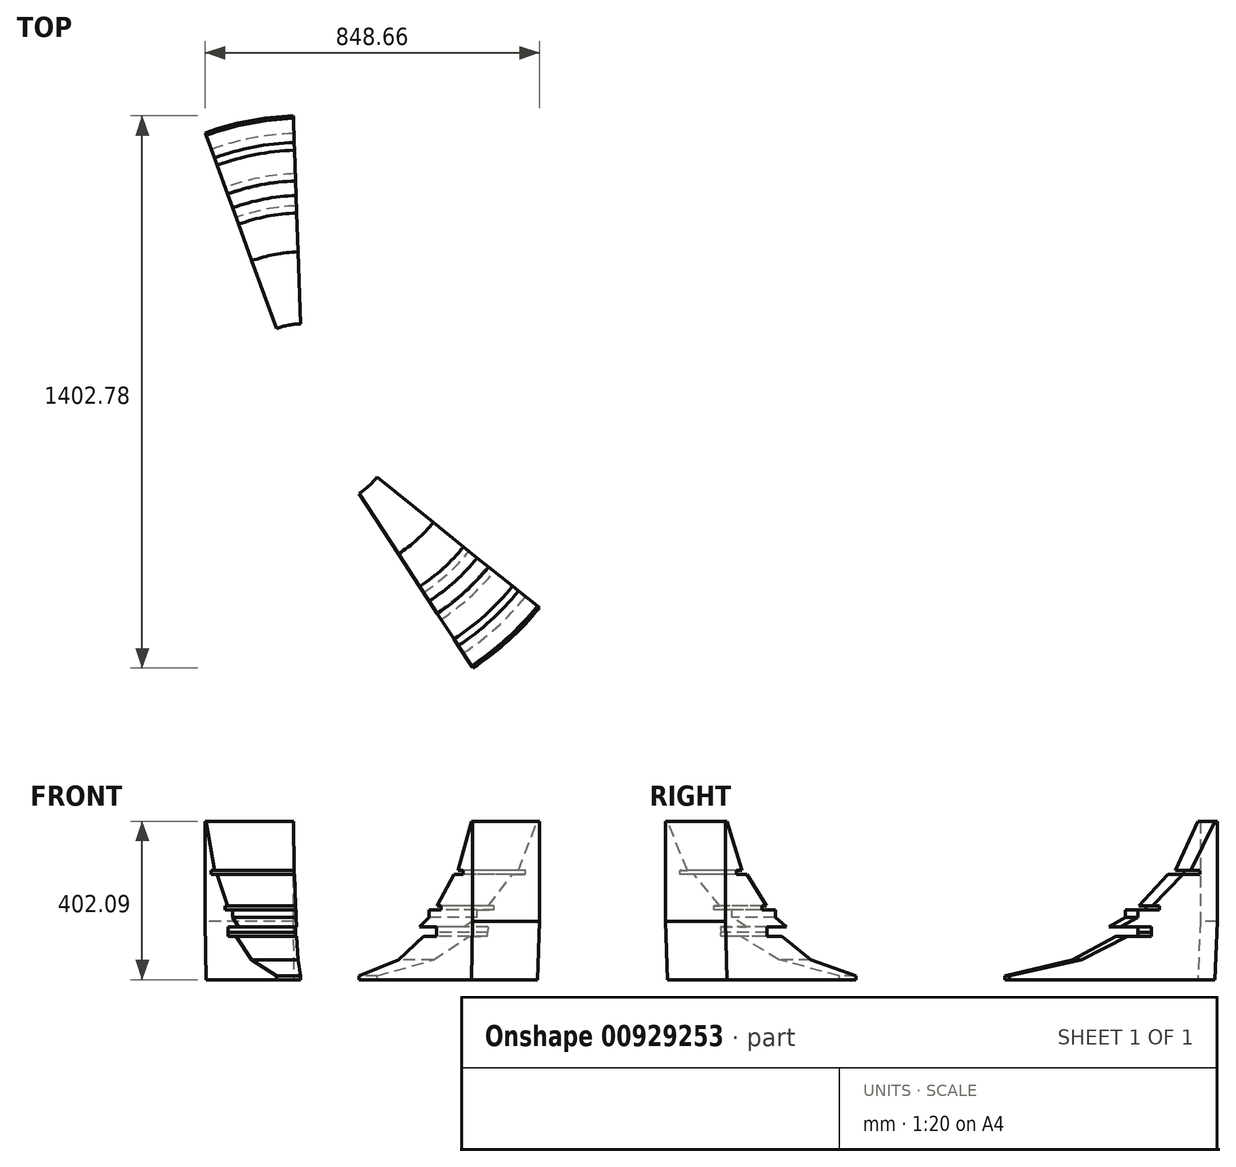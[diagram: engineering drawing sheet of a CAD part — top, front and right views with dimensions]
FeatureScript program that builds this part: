
annotation { "Feature Type Name" : "Feature", "Feature Type Description" : "" }
export const myFeature = defineFeature(function(context is Context, id is Id, definition is map)
    precondition{}
    {
        {
            var Q0;
            Q0=qCreatedBy(makeId("Front.planeOp"),FACE);
            var sketch = newSketch(context, id + "F0", { "sketchPlane" : qUnion([Q0])});
            skLineSegment(sketch, "E0", {"start": v(0, 0) * mm, "end": v(120, 0) * mm});
            skLineSegment(sketch, "E1", {"start": v(120, 0) * mm, "end": v(120, 10) * mm});
            skLineSegment(sketch, "E2.bottom", {"start": v(120, 10) * mm, "end": v(420, 10) * mm, "construction": true});
            skLineSegment(sketch, "E2.top", {"start": v(120, 110) * mm, "end": v(420, 110) * mm, "construction": true});
            skLineSegment(sketch, "E2.left", {"start": v(120, 10) * mm, "end": v(120, 110) * mm, "construction": true});
            skLineSegment(sketch, "E2.right", {"start": v(420, 10) * mm, "end": v(420, 110) * mm, "construction": true});
            skLineSegment(sketch, "E3", {"start": v(120, 10) * mm, "end": v(303.16, 50.16) * mm});
            skLineSegment(sketch, "E4", {"start": v(303.16, 50.16) * mm, "end": v(420, 110) * mm});
            skLineSegment(sketch, "E5", {"start": v(420, 110) * mm, "end": v(480.38, 110) * mm});
            skLineSegment(sketch, "E6", {"start": v(480.38, 110) * mm, "end": v(480.38, 119.71) * mm});
            skLineSegment(sketch, "E7", {"start": v(420, 134) * mm, "end": v(480.73, 134) * mm});
            skLineSegment(sketch, "E8", {"start": v(480.73, 134) * mm, "end": v(480.38, 119.71) * mm});
            skLineSegment(sketch, "E9", {"start": v(420, 134) * mm, "end": v(401.9, 134) * mm});
            skLineSegment(sketch, "E10", {"start": v(401.9, 134) * mm, "end": v(446.37, 158.34) * mm});
            skLineSegment(sketch, "E11", {"start": v(446.37, 158.34) * mm, "end": v(446.37, 177.2) * mm});
            skLineSegment(sketch, "E12", {"start": v(446.37, 177.2) * mm, "end": v(501.62, 177.2) * mm});
            skLineSegment(sketch, "E13", {"start": v(501.62, 177.2) * mm, "end": v(501.62, 187.3) * mm});
            skLineSegment(sketch, "E14", {"start": v(501.62, 187.3) * mm, "end": v(483.43, 187.3) * mm});
            skLineSegment(sketch, "E15", {"start": v(483.43, 187.3) * mm, "end": v(561.58, 268.16) * mm});
            skLineSegment(sketch, "E16", {"start": v(561.58, 268.16) * mm, "end": v(575.06, 268.16) * mm});
            skLineSegment(sketch, "E17", {"start": v(575.06, 268.16) * mm, "end": v(604.03, 268.16) * mm});
            skLineSegment(sketch, "E18", {"start": v(604.03, 268.16) * mm, "end": v(604.03, 277.45) * mm});
            skLineSegment(sketch, "E19", {"start": v(604.03, 277.45) * mm, "end": v(581.12, 277.45) * mm});
            skLineSegment(sketch, "E20", {"start": v(581.12, 277.45) * mm, "end": v(642.43, 402.09) * mm});
            skLineSegment(sketch, "E21", {"start": v(642.43, 402.09) * mm, "end": v(648.86, 402.09) * mm});
            skLineSegment(sketch, "E22", {"start": v(648.86, 402.09) * mm, "end": v(648.86, 148.71) * mm});
            skLineSegment(sketch, "E23", {"start": v(648.86, 148.71) * mm, "end": v(642.43, 0) * mm});
            skLineSegment(sketch, "E24", {"start": v(642.43, 0) * mm, "end": v(355.24, 0) * mm});
            skLineSegment(sketch, "E25", {"start": v(355.24, 0) * mm, "end": v(120, 0) * mm});
            skLineSegment(sketch, "E26", {"start": v(0, 0) * mm, "end": v(0, 125.67) * mm});
            skLineSegment(sketch, "E27", {"start": v(120, 0) * mm, "end": v(-80, 0) * mm});
            skLineSegment(sketch, "E28", {"start": v(-80, 0) * mm, "end": v(-80, 71.97) * mm});
            skSolve(sketch);
        }
        {
            var Q0;
            Q0=qCreatedBy(makeId("Top.planeOp"),FACE);
            cPlane(context, id + "F1", {"entities" : qUnion([Q0]), "cplaneType" : CPlaneType.OFFSET, "offset" : 100 * mm, "width" : 150 * mm, "height" : 150 * mm});
        }
        {
            var Q0;
            Q0=qCreatedBy(id+"F1.planeOp",FACE);
            var sketch = newSketch(context, id + "F2", { "sketchPlane" : qUnion([Q0])});
            skLineSegment(sketch, "E29.bottom", {"start": v(-120, 200) * mm, "end": v(120, 200) * mm});
            skLineSegment(sketch, "E29.top", {"start": v(-120, -200) * mm, "end": v(120, -200) * mm});
            skLineSegment(sketch, "E29.left", {"start": v(-120, 200) * mm, "end": v(-120, -200) * mm, "construction": true});
            skLineSegment(sketch, "E29.right", {"start": v(120, 200) * mm, "end": v(120, -200) * mm});
            skPoint(sketch, "E29.middle", {"position": v(0, 0) * mm});
            skLineSegment(sketch, "E30", {"start": v(466.33, 0) * mm, "end": v(466.33, 144.24) * mm});
            skLineSegment(sketch, "E31", {"start": v(466.33, 0) * mm, "end": v(120, 0) * mm, "construction": true});
            skLineSegment(sketch, "E32", {"start": v(0, 200) * mm, "end": v(0, 546.33) * mm, "construction": true});
            skLineSegment(sketch, "E33", {"start": v(0, 546.33) * mm, "end": v(74.47, 546.33) * mm});
            skLineSegment(sketch, "E34", {"start": v(74.47, 546.33) * mm, "end": v(183.07, 524.3) * mm});
            skLineSegment(sketch, "E35", {"start": v(183.07, 524.3) * mm, "end": v(318.83, 440.9) * mm});
            skLineSegment(sketch, "E36", {"start": v(318.83, 440.9) * mm, "end": v(427.44, 303.21) * mm});
            skLineSegment(sketch, "E37", {"start": v(427.44, 303.21) * mm, "end": v(466.33, 233.4) * mm});
            skLineSegment(sketch, "E38", {"start": v(466.33, 233.4) * mm, "end": v(466.33, 144.24) * mm});
            skLineSegment(sketch, "E39.bottom", {"start": v(0, 0) * mm, "end": v(80, 0) * mm});
            skLineSegment(sketch, "E39.top", {"start": v(0, -80) * mm, "end": v(80, -80) * mm, "construction": true});
            skLineSegment(sketch, "E39.left", {"start": v(0, 0) * mm, "end": v(0, -80) * mm});
            skLineSegment(sketch, "E39.right", {"start": v(80, 0) * mm, "end": v(80, -80) * mm});
            skLineSegment(sketch, "E40", {"start": v(80, -80) * mm, "end": v(0, 0) * mm, "construction": true});
            skLineSegment(sketch, "E41", {"start": v(0, 0) * mm, "end": v(80, 80) * mm, "construction": true});
            skLineSegment(sketch, "E42", {"start": v(0, 0) * mm, "end": v(40, -80) * mm});
            skSolve(sketch);
        }
        {
            var Q0;
            Q0=makeQuery(id+"F0.imprint","IMPRINT",FACE,{"disambiguationData":[TD([[makeQuery(id+"F0.imprint","IMPRINT",EDGE,{"derivedFrom":sQuery(id+"F0.wireOp",EDGE,"E1")}),-1.0]])]});
            var Q1;
            Q1=sQuery(id+"F0.wireOp",EDGE,"E28");
            revolve(context, id + "F3", {"surfaceOperationType" : NewSurfaceOperationType.NEW, "entities" : qUnion([Q0]), "axis" : qUnion([Q1]), "revolveType" : RevolveType.TWO_DIRECTIONS, "oppositeDirection" : true, "angle" : 268 * degree, "angleBack" : 250 * degree});
        }
        {
            var Q0;
            Q0=sQuery(id+"F2.wireOp",VERTEX,"E29.middle");
            var Q1;
            Q1=sQuery(id+"F2.wireOp",EDGE,"E42");
            cPlane(context, id + "F4", {"entities" : qUnion([Q0, Q1]), "cplaneType" : CPlaneType.CURVE_POINT, "offset" : 25 * mm, "width" : 150 * mm, "height" : 150 * mm});
        }
        {
            var Q0;
            Q0=makeQuery(id+"F3.opRevolve","SWEPT_BODY",BODY,{"disambiguationData":[OSD([sQuery(id+"F0.wireOp",EDGE,"E1"),sQuery(id+"F0.wireOp",EDGE,"E3"),sQuery(id+"F0.wireOp",EDGE,"E4"),sQuery(id+"F0.wireOp",EDGE,"E5"),sQuery(id+"F0.wireOp",EDGE,"E6"),sQuery(id+"F0.wireOp",EDGE,"E7"),sQuery(id+"F0.wireOp",EDGE,"E8"),sQuery(id+"F0.wireOp",EDGE,"E9"),sQuery(id+"F0.wireOp",EDGE,"E10"),sQuery(id+"F0.wireOp",EDGE,"E11"),sQuery(id+"F0.wireOp",EDGE,"E12"),sQuery(id+"F0.wireOp",EDGE,"E13"),sQuery(id+"F0.wireOp",EDGE,"E14"),sQuery(id+"F0.wireOp",EDGE,"E15"),sQuery(id+"F0.wireOp",EDGE,"E16"),sQuery(id+"F0.wireOp",EDGE,"E17"),sQuery(id+"F0.wireOp",EDGE,"E18"),sQuery(id+"F0.wireOp",EDGE,"E19"),sQuery(id+"F0.wireOp",EDGE,"E20"),sQuery(id+"F0.wireOp",EDGE,"E21"),sQuery(id+"F0.wireOp",EDGE,"E22"),sQuery(id+"F0.wireOp",EDGE,"E23"),sQuery(id+"F0.wireOp",EDGE,"E24"),sQuery(id+"F0.wireOp",EDGE,"E25")])]});
            var Q1;
            Q1=qCreatedBy(id+"F4.planeOp",FACE);
            mirror(context, id + "F5", {"entities" : qUnion([Q0]), "mirrorPlane" : qUnion([Q1])});
        }
    });
